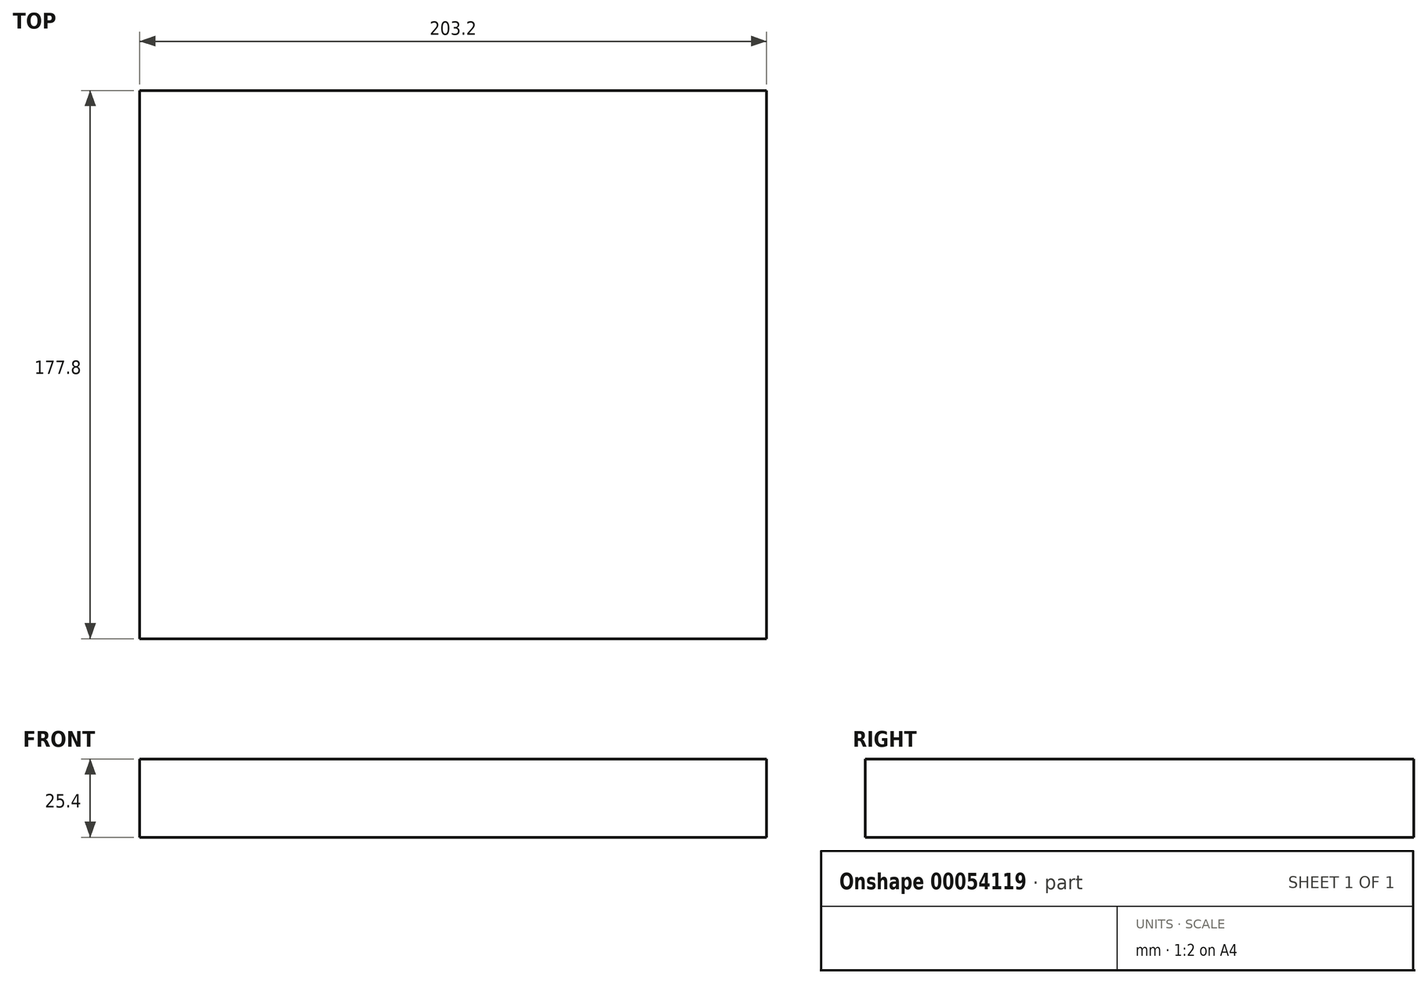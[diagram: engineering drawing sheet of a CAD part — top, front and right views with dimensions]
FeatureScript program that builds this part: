
annotation { "Feature Type Name" : "Feature", "Feature Type Description" : "" }
export const myFeature = defineFeature(function(context is Context, id is Id, definition is map)
    precondition{}
    {
        {
            var Q0;
            Q0=qCreatedBy(makeId("Top.planeOp"),FACE);
            var sketch = newSketch(context, id + "F0", { "sketchPlane" : qUnion([Q0])});
            skLineSegment(sketch, "E0.rect.bottom", {"start": v(101.6, -88.9) * mm, "end": v(-101.6, -88.9) * mm});
            skLineSegment(sketch, "E0.rect.top", {"start": v(101.6, 88.9) * mm, "end": v(-101.6, 88.9) * mm});
            skLineSegment(sketch, "E0.rect.left", {"start": v(101.6, -88.9) * mm, "end": v(101.6, 88.9) * mm});
            skLineSegment(sketch, "E0.rect.right", {"start": v(-101.6, -88.9) * mm, "end": v(-101.6, 88.9) * mm});
            skPoint(sketch, "E0.rect.middle", {"position": v(0, 0) * mm});
            skSolve(sketch);
        }
        {
            var Q0;
            Q0 = qSketchRegion(id + "F0", true);
            extrude(context, id + "F1", {"entities" : qUnion([Q0]), "depth" : 25.4 * mm});
        }
    });
